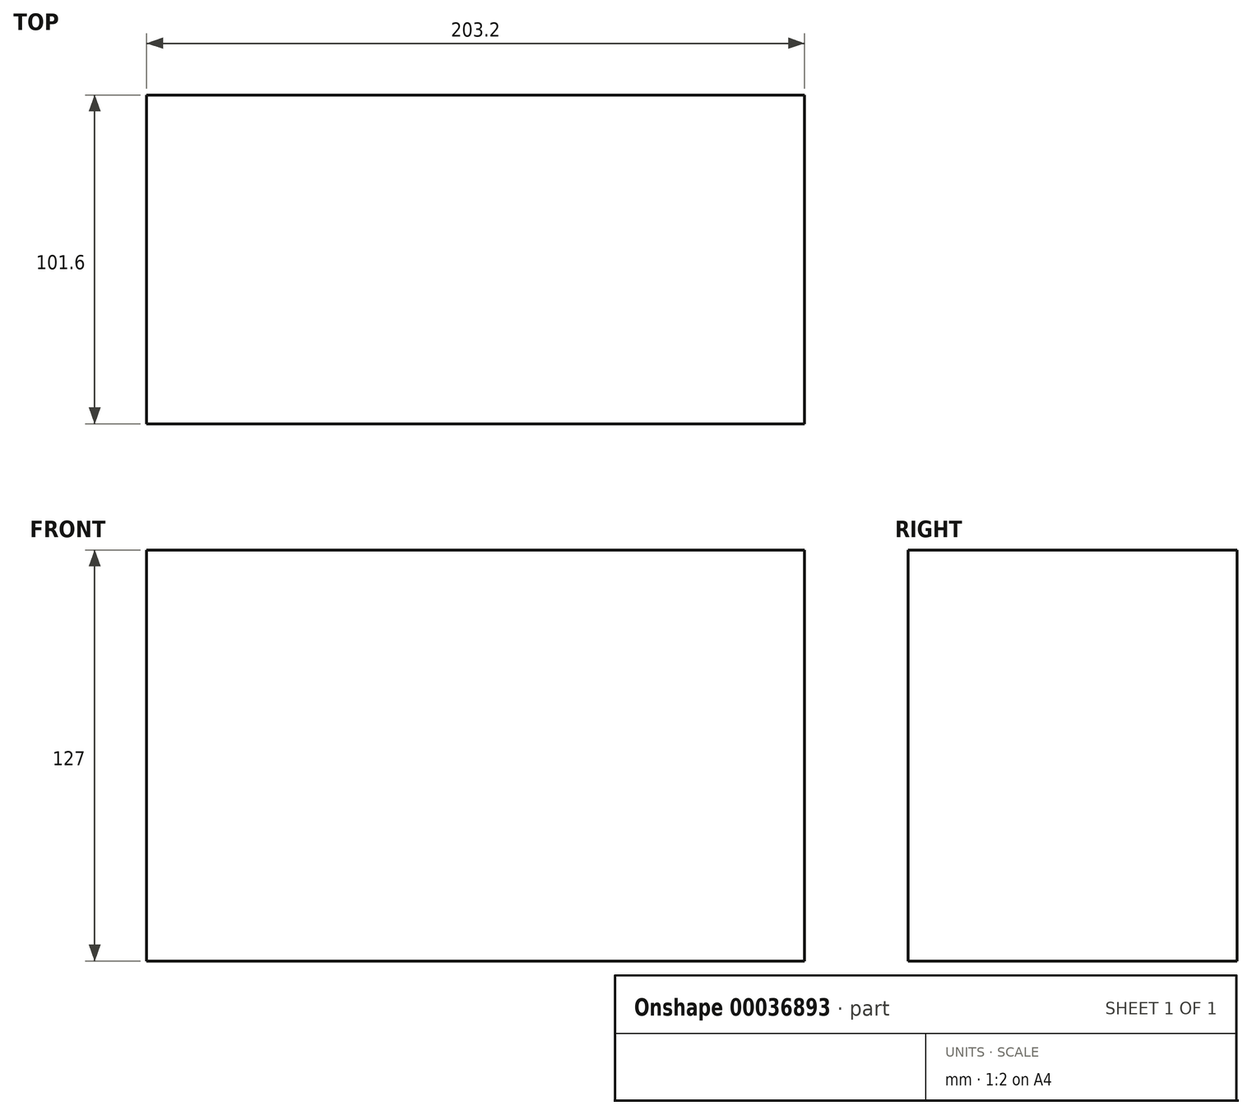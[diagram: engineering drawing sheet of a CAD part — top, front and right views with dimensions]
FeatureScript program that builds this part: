
annotation { "Feature Type Name" : "Feature", "Feature Type Description" : "" }
export const myFeature = defineFeature(function(context is Context, id is Id, definition is map)
    precondition{}
    {
        {
            var Q0;
            Q0=qCreatedBy(makeId("Top.planeOp"),FACE);
            var sketch = newSketch(context, id + "F0", { "sketchPlane" : qUnion([Q0])});
            skLineSegment(sketch, "E0.bottom", {"start": v(-71.76, -56.06) * mm, "end": v(131.44, -56.06) * mm});
            skLineSegment(sketch, "E0.top", {"start": v(-71.76, 45.54) * mm, "end": v(131.44, 45.54) * mm});
            skLineSegment(sketch, "E0.left", {"start": v(-71.76, -56.06) * mm, "end": v(-71.76, 45.54) * mm});
            skLineSegment(sketch, "E0.right", {"start": v(131.44, -56.06) * mm, "end": v(131.44, 45.54) * mm});
            skSolve(sketch);
        }
        {
            var Q0;
            Q0=makeQuery(id+"F0.imprint","IMPRINT",FACE,{"disambiguationData":[TD([[makeQuery(id+"F0.imprint","IMPRINT",EDGE,{"derivedFrom":sQuery(id+"F0.wireOp",EDGE,"E0.bottom")}),1.0]])]});
            extrude(context, id + "F1", {"entities" : qUnion([Q0]), "depth" : 127 * mm});
        }
    });
